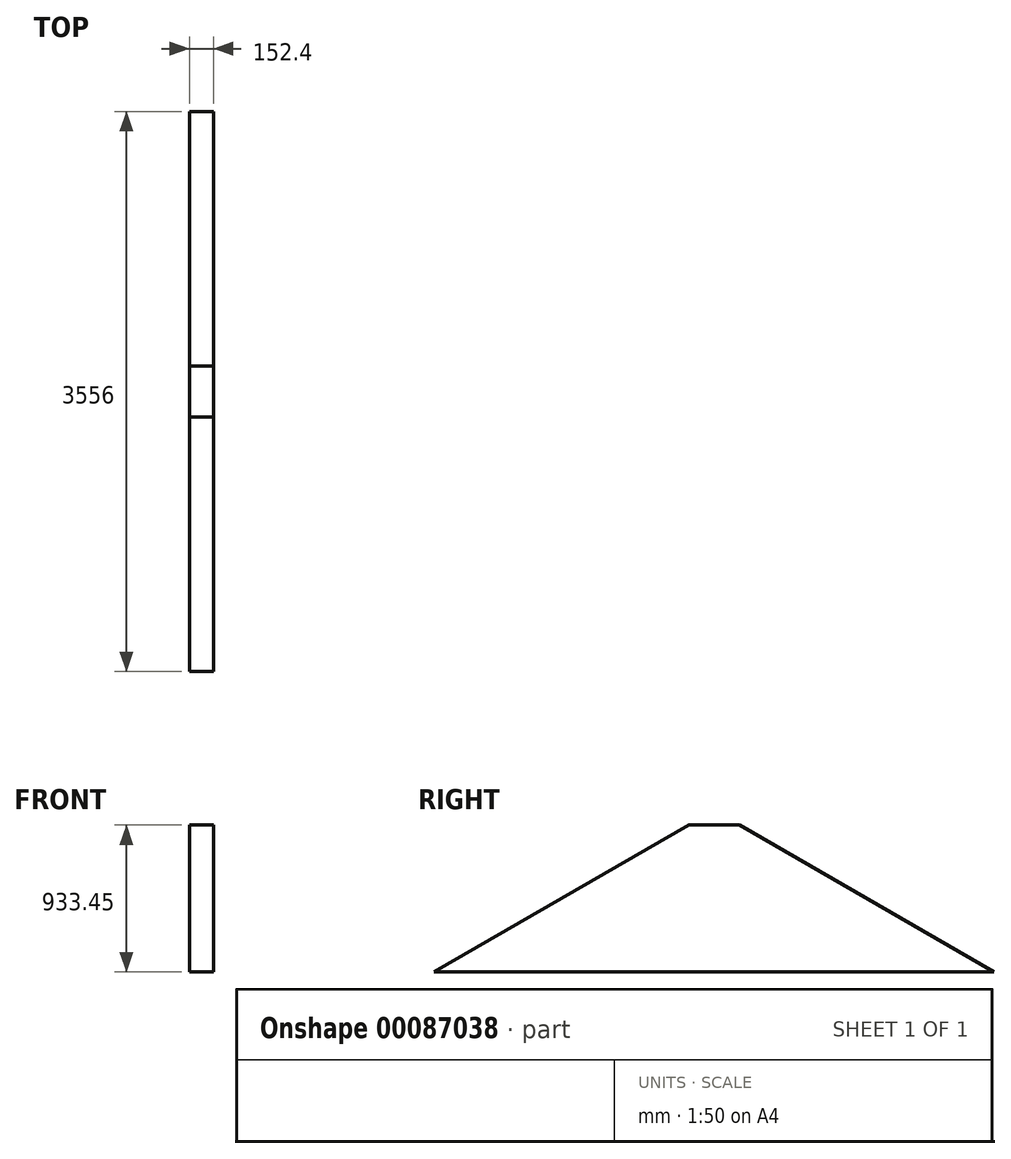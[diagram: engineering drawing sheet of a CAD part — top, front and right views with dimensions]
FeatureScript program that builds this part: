
annotation { "Feature Type Name" : "Feature", "Feature Type Description" : "" }
export const myFeature = defineFeature(function(context is Context, id is Id, definition is map)
    precondition{}
    {
        {
            var Q0;
            Q0=qCreatedBy(makeId("Right.planeOp"),FACE);
            var sketch = newSketch(context, id + "F0", { "sketchPlane" : qUnion([Q0])});
            skLineSegment(sketch, "E0", {"start": v(-1778, 0) * mm, "end": v(-161.22, 933.45) * mm});
            skLineSegment(sketch, "E1", {"start": v(-161.22, 933.45) * mm, "end": v(161.22, 933.45) * mm});
            skLineSegment(sketch, "E2", {"start": v(161.22, 933.45) * mm, "end": v(1778, 0) * mm});
            skLineSegment(sketch, "E3", {"start": v(1778, 0) * mm, "end": v(-1778, 0) * mm});
            skPoint(sketch, "E4", {"position": v(0, 0) * mm});
            skSolve(sketch);
        }
        {
            var Q0;
            Q0=makeQuery(id+"F0.imprint","IMPRINT",FACE,{"disambiguationData":[TD([[makeQuery(id+"F0.imprint","IMPRINT",EDGE,{"derivedFrom":sQuery(id+"F0.wireOp",EDGE,"E0")}),-1.0]])]});
            extrude(context, id + "F1", {"entities" : qUnion([Q0]), "depth" : 152.4 * mm});
        }
    });
